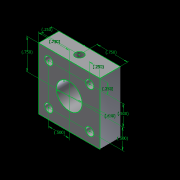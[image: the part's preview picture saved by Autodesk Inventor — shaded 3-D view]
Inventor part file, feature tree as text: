
AUTODESK INVENTOR PART (.ipt)
format: ipt  version: 2012 (Build 160160000, 160)  size: 122,880 bytes
history: native  units: in
note: dims shown in document units (in); Inventor stores cm internally (conversion verified against a paired STEP export)
features: hole x6, sketch x3, extrude x1
ambient origin geometry x8: Origin, YZ Plane, XZ Plane, XY Plane, X Axis, Y Axis, Z Axis, Center Point
bodies: Solid1 (feature_tree)
feature tree (10):
  extrude  "Extrusion1"  Depth=1.5in
  hole  "Hole1"  [1 undecoded]
  hole  "Hole2"  [1 undecoded]
  hole  "Hole3"  [1 undecoded]
  hole  "Hole4"  [1 undecoded]
  hole  "Hole5"  [1 undecoded]
  hole  "Hole6"  [1 undecoded]
  sketch  "Sketch2"  dims[d2=0.5in d3=0.0in d4=0.75in d5=0.75in]
  sketch  "Sketch3"  dims[d6=0.6299in d7=0.75in d8=0.375in d9=0.25in d10=0.5635in d11=1.0in d12=0.8108in d13=0.25in d14=0.25in d15=0.2in d16=0.75in d17=0.375in d18=0.25in d19=0.5635in d20=1.0in d21=0.8108in d22=0.25in d23=0.25in d24=0.2in d25=0.75in d26=0.375in d27=0.25in d28=0.5635in d29=1.0in d30=0.8108in d31=0.25in d32=0.25in d33=0.2in d34=0.75in d35=0.375in d36=0.25in d37=0.5635in d38=1.0in d39=0.8108in d40=0.25in d41=0.25in d42=0.2in d43=0.75in d44=0.375in d45=0.25in d46=0.5635in d47=1.0in d48=0.8108in d49=0.25in d50=0.75in d51=0.2in d52=0.75in d53=0.375in d54=0.25in d55=0.5635in d56=0.5in d57=0.8108in d58=0.25in d59=0.25in d60=0.75in d61=0.75in d62=0.25in d63=0.75in d64=0.6299in d65=0.5in d66=0.5in d67=0.5in]
  sketch  "Sketch1"  dims[d0=1.5in d1=1.5in]
note: 6 required parameter values undecoded (feature->parameter linkage not recoverable at this tier; creation-order binding heuristic only, values carry confidence <= 0.55)
